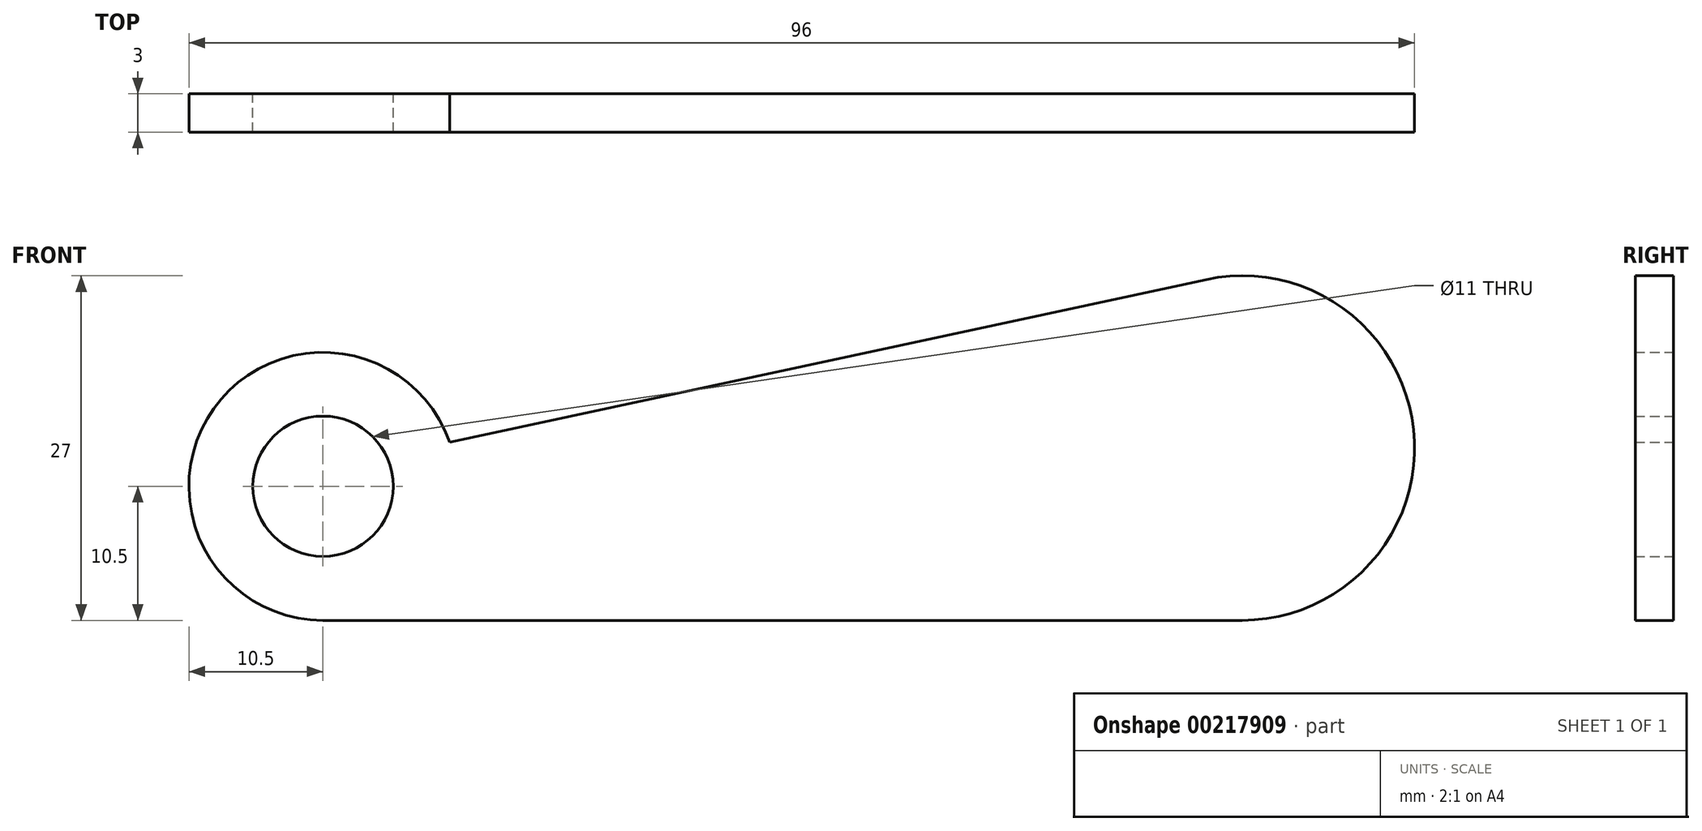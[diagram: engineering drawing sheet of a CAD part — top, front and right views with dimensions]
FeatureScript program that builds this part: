
annotation { "Feature Type Name" : "Feature", "Feature Type Description" : "" }
export const myFeature = defineFeature(function(context is Context, id is Id, definition is map)
    precondition{}
    {
        {
            var Q0;
            Q0=qCreatedBy(makeId("Front.planeOp"),FACE);
            var sketch = newSketch(context, id + "F0", { "sketchPlane" : qUnion([Q0])});
            skArc(sketch, "E0", {"start": v(0, -13.5) * mm, "mid": v(13.42, 1.43) * mm, "end": v(-2.84, 13.2) * mm});
            skLineSegment(sketch, "E1", {"start": v(0, -13.5) * mm, "end": v(-72, -13.5) * mm});
            skArc(sketch, "E2", {"start": v(-62.08, 0.45) * mm, "mid": v(-80.56, 3.08) * mm, "end": v(-72, -13.5) * mm});
            skLineSegment(sketch, "E3", {"start": v(-62.08, 0.45) * mm, "end": v(0, 13.8) * mm});
            skCircle(sketch, "E4", {"center": v(-72, -3) * mm, "radius": 5.5 * mm});
            skSolve(sketch);
        }
        {
            var Q0;
            Q0 = qSketchRegion(id + "F0", true);
            extrude(context, id + "F1", {"entities" : qUnion([Q0]), "depth" : 3 * mm});
        }
    });
